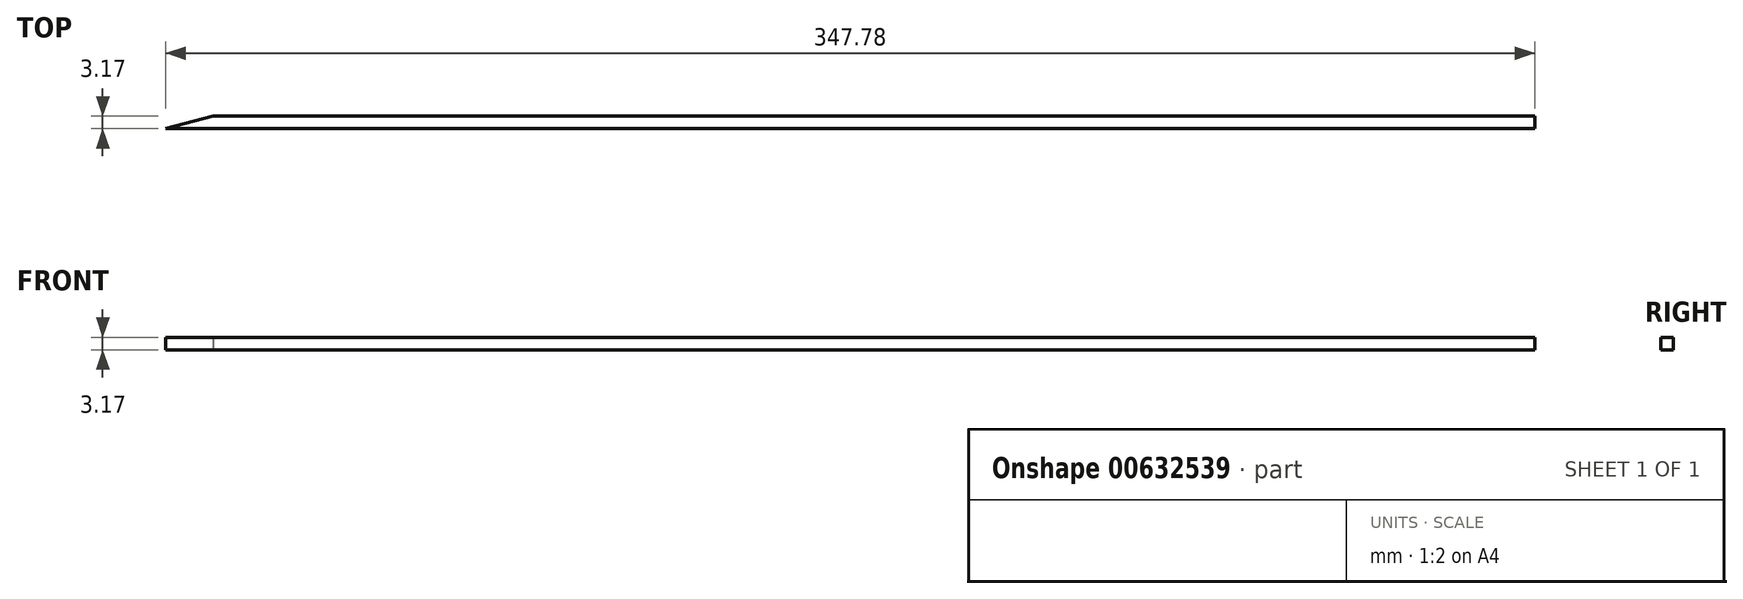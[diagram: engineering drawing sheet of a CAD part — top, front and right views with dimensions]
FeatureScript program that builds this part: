
annotation { "Feature Type Name" : "Feature", "Feature Type Description" : "" }
export const myFeature = defineFeature(function(context is Context, id is Id, definition is map)
    precondition{}
    {
        {
            var Q0;
            Q0=qCreatedBy(makeId("Top.planeOp"),FACE);
            var sketch = newSketch(context, id + "F0", { "sketchPlane" : qUnion([Q0])});
            skLineSegment(sketch, "E0", {"start": v(-146.37, 5.91) * mm, "end": v(189.4, 5.91) * mm});
            skLineSegment(sketch, "E1", {"start": v(189.4, 5.91) * mm, "end": v(189.4, 2.74) * mm});
            skLineSegment(sketch, "E2", {"start": v(189.4, 2.74) * mm, "end": v(-158.37, 2.74) * mm});
            skLineSegment(sketch, "E3", {"start": v(-158.37, 2.74) * mm, "end": v(-146.37, 5.91) * mm});
            skSolve(sketch);
        }
        {
            var Q0;
            Q0=qSketchRegion(id+"F0",true);
            extrude(context, id + "F1", {"entities" : qUnion([Q0]), "depth" : 3.17 * mm, "offsetDistance" : 25.4 * mm});
        }
    });
